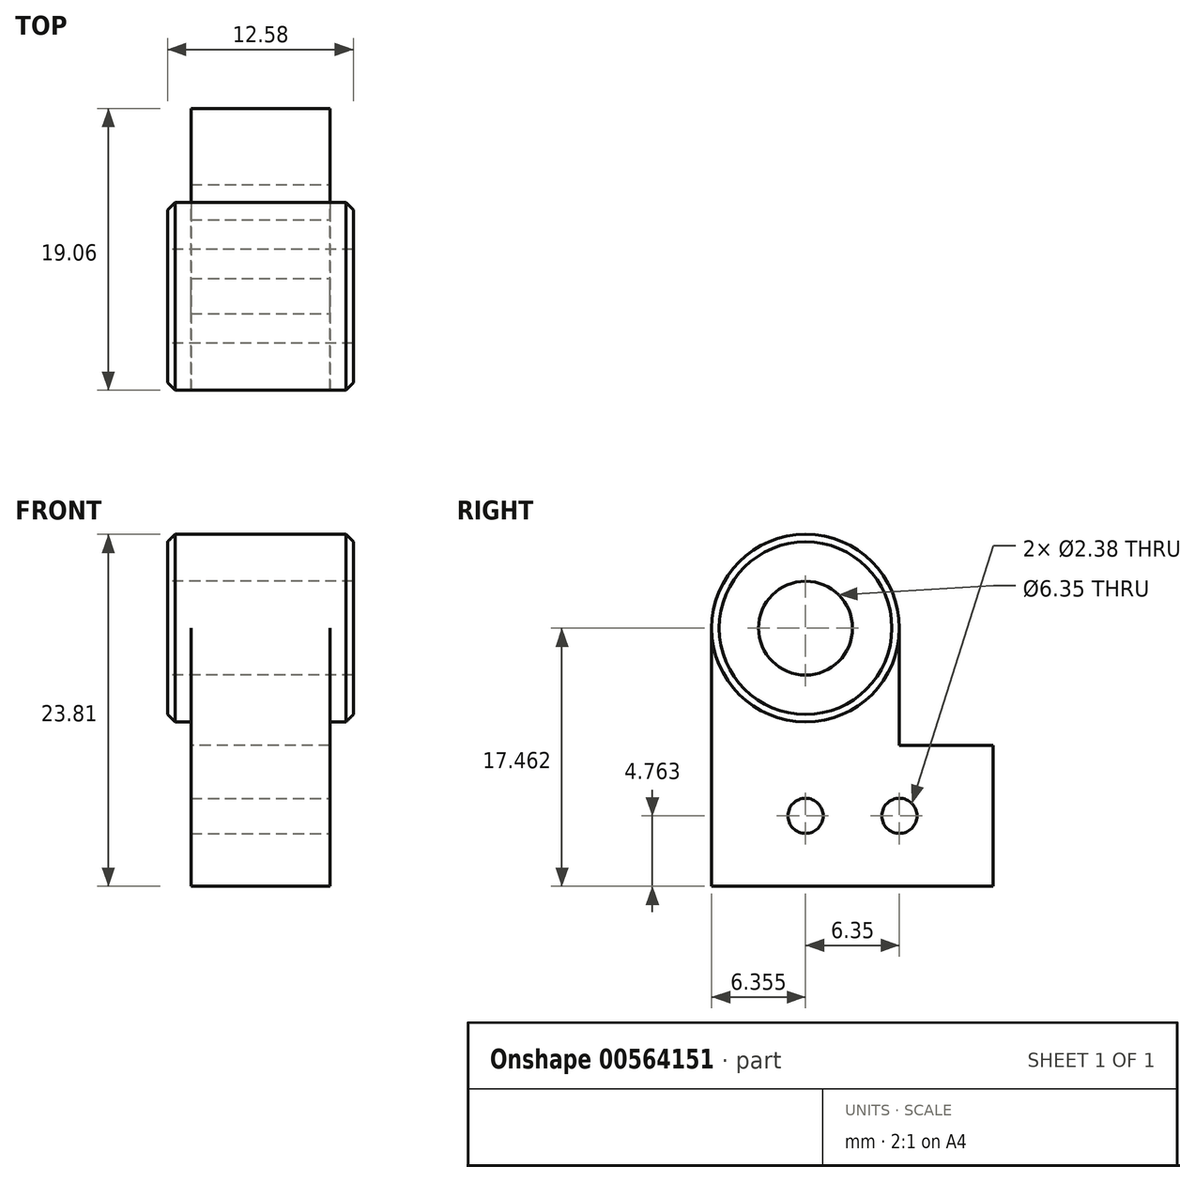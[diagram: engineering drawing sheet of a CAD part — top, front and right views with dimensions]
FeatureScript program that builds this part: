
annotation { "Feature Type Name" : "Feature", "Feature Type Description" : "" }
export const myFeature = defineFeature(function(context is Context, id is Id, definition is map)
    precondition{}
    {
        {
            var Q0;
            Q0=qCreatedBy(makeId("Right.planeOp"),FACE);
            var sketch = newSketch(context, id + "F0", { "sketchPlane" : qUnion([Q0])});
            skLineSegment(sketch, "E0.bottom", {"start": v(9.53, 0) * mm, "end": v(-9.52, 0) * mm});
            skLineSegment(sketch, "E0.top", {"start": v(9.53, 9.52) * mm, "end": v(-9.52, 9.52) * mm});
            skLineSegment(sketch, "E0.left", {"start": v(9.53, 0) * mm, "end": v(9.53, 9.52) * mm});
            skLineSegment(sketch, "E0.right", {"start": v(-9.52, 0) * mm, "end": v(-9.52, 9.52) * mm});
            skPoint(sketch, "E1", {"position": v(0, 0) * mm});
            skSolve(sketch);
        }
        {
            var Q0;
            Q0=qSketchRegion(id+"F0",true);
            extrude(context, id + "F1", {"entities" : qUnion([Q0]), "depth" : 4.76 * mm - 0.06 * mm, "offsetDistance" : 25.4 * mm});
        }
        {
            var Q0;
            Q0=qCreatedBy(makeId("Right.planeOp"),FACE);
            var sketch = newSketch(context, id + "F2", { "sketchPlane" : qUnion([Q0])});
            skCircle(sketch, "E2", {"center": v(-3.17, 17.46) * mm, "radius": 6.35 * mm});
            skCircle(sketch, "E3", {"center": v(-3.17, 17.46) * mm, "radius": 3.18 * mm});
            skLineSegment(sketch, "E4", {"start": v(-10.81, 0) * mm, "end": v(-10.81, 9.53) * mm});
            skPoint(sketch, "E5", {"position": v(-10.81, 4.76) * mm});
            skLineSegment(sketch, "E6", {"start": v(-9.52, 0) * mm, "end": v(-9.52, 17.46) * mm});
            skLineSegment(sketch, "E7", {"start": v(3.18, 17.46) * mm, "end": v(3.18, 0) * mm});
            skLineSegment(sketch, "E8", {"start": v(3.18, 0) * mm, "end": v(-9.52, 0) * mm});
            skSolve(sketch);
        }
        {
            var Q0;
            Q0=qSketchRegion(id+"F2",true);
            extrude(context, id + "F3", {"entities" : qUnion([Q0]), "operationType" : NewBodyOperationType.ADD, "depth" : 4.76 * mm - 0.06 * mm, "offsetDistance" : 25.4 * mm});
        }
        {
            var Q0;
            Q0=makeQuery(id+"F1.opExtrude","CAP_FACE",FACE,{"disambiguationData":[OSD([sQuery(id+"F0.wireOp",EDGE,"E0.bottom"),sQuery(id+"F0.wireOp",EDGE,"E0.top"),sQuery(id+"F0.wireOp",EDGE,"E0.left"),sQuery(id+"F0.wireOp",EDGE,"E0.right")])],"isStart":false});
            var sketch = newSketch(context, id + "F4", { "sketchPlane" : qUnion([Q0])});
            skCircle(sketch, "E9", {"center": v(-3.17, 4.76) * mm, "radius": 1.2 * mm});
            skCircle(sketch, "E10.MirrorC", {"center": v(3.18, 4.76) * mm, "radius": 1.2 * mm});
            skPoint(sketch, "E11", {"position": v(-9.52, 8.73) * mm});
            skSolve(sketch);
        }
        {
            var Q0;
            Q0=qSketchRegion(id+"F4",true);
            extrude(context, id + "F5", {"entities" : qUnion([Q0]), "operationType" : NewBodyOperationType.REMOVE, "endBound" : BoundingType.THROUGH_ALL, "oppositeDirection" : true, "depth" : 25.4 * mm, "offsetDistance" : 25.4 * mm});
        }
        {
            var Q0;
            Q0=makeQuery(id+"F3.boolean.opBoolean","MERGE",FACE,{"derivedFrom":[makeQuery(id+"F1.opExtrude","CAP_FACE",FACE,{"disambiguationData":[OSD([sQuery(id+"F0.wireOp",EDGE,"E0.bottom"),sQuery(id+"F0.wireOp",EDGE,"E0.top"),sQuery(id+"F0.wireOp",EDGE,"E0.left"),sQuery(id+"F0.wireOp",EDGE,"E0.right")])],"isStart":false}),makeQuery(id+"F3.opExtrude","CAP_FACE",FACE,{"disambiguationData":[OSD([sQuery(id+"F2.wireOp",EDGE,"E2"),sQuery(id+"F2.wireOp",EDGE,"E3"),sQuery(id+"F2.wireOp",EDGE,"E6"),sQuery(id+"F2.wireOp",EDGE,"E7"),sQuery(id+"F2.wireOp",EDGE,"E8")])],"isStart":false})]});
            var sketch = newSketch(context, id + "F6", { "sketchPlane" : qUnion([Q0])});
            skCircle(sketch, "E12", {"center": v(-3.17, 17.46) * mm, "radius": 6.35 * mm});
            skCircle(sketch, "E13", {"center": v(-3.17, 17.46) * mm, "radius": 3.18 * mm});
            skSolve(sketch);
        }
        {
            var Q0;
            Q0 = qSketchRegion(id + "F6", true);
            extrude(context, id + "F7", {"entities" : qUnion([Q0]), "operationType" : NewBodyOperationType.ADD, "depth" : 1.59 * mm, "offsetDistance" : 25.4 * mm});
        }
        {
            var Q0;
            Q0=makeQuery(id+"F1.opExtrude","SWEPT_BODY",BODY,{"disambiguationData":[OSD([sQuery(id+"F0.wireOp",EDGE,"E0.bottom"),sQuery(id+"F0.wireOp",EDGE,"E0.top"),sQuery(id+"F0.wireOp",EDGE,"E0.left"),sQuery(id+"F0.wireOp",EDGE,"E0.right")])]});
            var Q1;
            Q1=qCreatedBy(makeId("Right.planeOp"),FACE);
            mirror(context, id + "F8", {"operationType" : NewBodyOperationType.ADD, "entities" : qUnion([Q0]), "mirrorPlane" : qUnion([Q1])});
        }
        {
            var Q0;
            Q0=makeQuery(id+"F7.opExtrude","CAP_EDGE",EDGE,{"disambiguationData":[OSD([sQuery(id+"F6.wireOp",EDGE,"E12")])],"isStart":false});
            var Q1;
            Q1=makeQuery(id+"F8.opPattern","COPY",EDGE,{"derivedFrom":makeQuery(id+"F7.opExtrude","CAP_EDGE",EDGE,{"disambiguationData":[OSD([sQuery(id+"F6.wireOp",EDGE,"E12")])],"isStart":false}),"instanceName":"1"});
            chamfer(context, id + "F9", {"entities" : qUnion([Q0, Q1]), "width" : 0.5 * mm, "tangentPropagation" : true});
        }
    });
